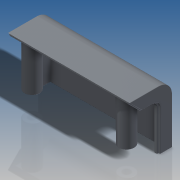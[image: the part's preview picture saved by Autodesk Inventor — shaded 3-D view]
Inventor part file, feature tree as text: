
AUTODESK INVENTOR PART (.ipt)
format: ipt  version: 2016 SP2 (Build 200236200, 236)  size: 273,408 bytes
history: native  units: in
note: dims shown in document units (in); Inventor stores cm internally (conversion verified against a paired STEP export)
features: extrude x4, sketch x3, plane x1, mirror x1, fillet x1
ambient origin geometry x8: Origin, YZ Plane, XZ Plane, XY Plane, X Axis, Y Axis, Z Axis, Center Point
bodies: Solid1 (feature_tree)
feature tree (10):
  sketch  "Sketch2"  dims[d0=0.1417in d1=0.0472in]
  extrude  "Extrusion1"  Depth=0.0472in
  extrude  "Extrusion2"  Depth=0.0472in
  plane  "Work Plane1"
  extrude  "Extrusion3"  Depth=0.0039in
  extrude  "Extrusion4"  Depth=0.0039in
  mirror  "Mirror1"
  fillet  "Fillet1"  Radius=0.1417in
  sketch  "Sketch3"  dims[d2=45.0deg d3=0.0472in]
  sketch  "Sketch4"  dims[d4=0.1417in d5=0.6142in d6=0.0157in d7=0.1417in d9=0.4409in d10=1.2598in d11=0.0in d12=1.1654in d13=0.0in d14=0.4409in d15=0.9764in d16=0.1575in d17=0.0787in d18=0.2835in d19=1.1654in d20=0.0in d21=0.0157in d22=0.0157in d23=0.0in d24=0.0039in]
